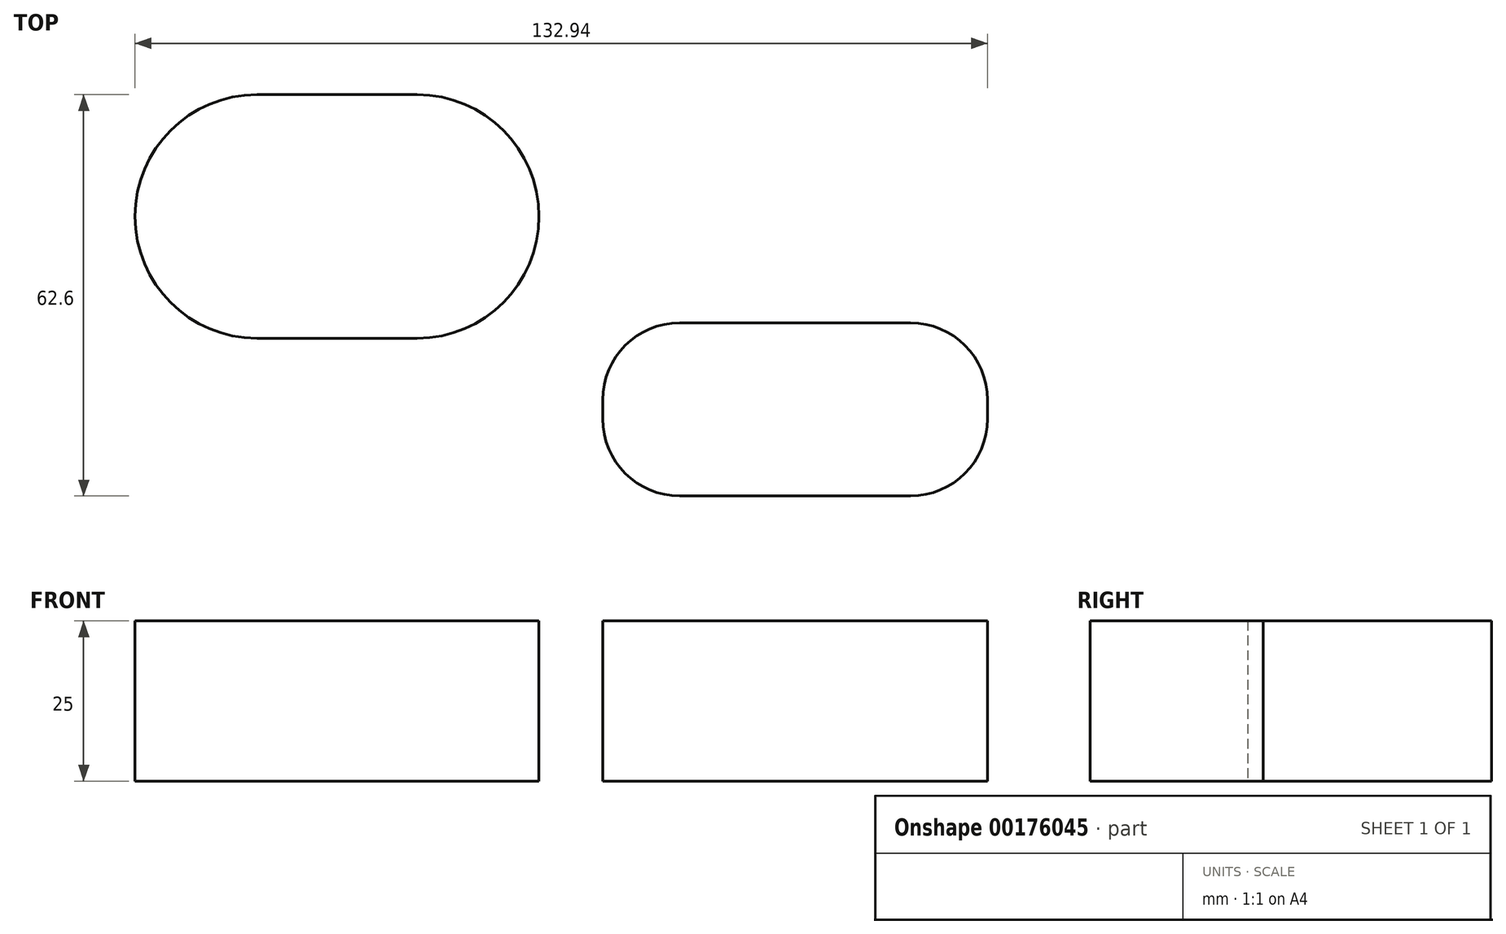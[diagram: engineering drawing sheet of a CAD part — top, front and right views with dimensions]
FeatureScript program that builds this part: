
annotation { "Feature Type Name" : "Feature", "Feature Type Description" : "" }
export const myFeature = defineFeature(function(context is Context, id is Id, definition is map)
    precondition{}
    {
        {
            var Q0;
            Q0=qCreatedBy(makeId("Top.planeOp"),FACE);
            var sketch = newSketch(context, id + "F0", { "sketchPlane" : qUnion([Q0])});
            skCircle(sketch, "E0", {"center": v(-13.87, 0) * mm, "radius": 19 * mm});
            skCircle(sketch, "E1", {"center": v(11.13, 0) * mm, "radius": 19 * mm});
            skLineSegment(sketch, "E2", {"start": v(-13.87, 19) * mm, "end": v(11.13, 19) * mm});
            skLineSegment(sketch, "E3", {"start": v(11.13, -19) * mm, "end": v(-13.87, -19) * mm});
            skSolve(sketch);
        }
        {
            var Q0;
            Q0 = qSketchRegion(id + "F0", true);
            var Q1;
            {var subQ0=sQuery(id+"F0.wireOp",EDGE,"E1");var subQ1=sQuery(id+"F0.wireOp",EDGE,"E0");var subQ2=makeQuery(id+"F0.imprint","INTERSECT",VERTEX,{"disambiguationData":[OD(0.0)],"derivedFrom":[subQ1,subQ0]});Q1=makeQuery(id+"F0.imprint","IMPRINT",FACE,{"disambiguationData":[TD([[makeQuery(id+"F0.imprint","IMPRINT",EDGE,{"disambiguationData":[TD([[subQ2,1.0]])],"derivedFrom":subQ1}),1.0]])]});}
            extrude(context, id + "F1", {"entities" : qUnion([Q0, Q1]), "depth" : 25 * mm});
        }
        {
            var Q0;
            Q0=qCreatedBy(makeId("Top.planeOp"),FACE);
            var sketch = newSketch(context, id + "F2", { "sketchPlane" : qUnion([Q0])});
            skCircle(sketch, "E4", {"center": v(52.07, -31.6) * mm, "radius": 12 * mm});
            skCircle(sketch, "E5", {"center": v(52.07, -28.6) * mm, "radius": 12 * mm});
            skCircle(sketch, "E6", {"center": v(88.07, -28.6) * mm, "radius": 12 * mm});
            skCircle(sketch, "E7", {"center": v(88.07, -31.6) * mm, "radius": 12 * mm});
            skLineSegment(sketch, "E8", {"start": v(52.07, -16.6) * mm, "end": v(88.07, -16.6) * mm});
            skLineSegment(sketch, "E9", {"start": v(100.07, -28.6) * mm, "end": v(100.07, -31.6) * mm});
            skLineSegment(sketch, "E10", {"start": v(52.07, -43.6) * mm, "end": v(88.07, -43.6) * mm});
            skLineSegment(sketch, "E11", {"start": v(40.07, -28.6) * mm, "end": v(40.07, -31.6) * mm});
            skSolve(sketch);
        }
        {
            var Q0;
            Q0 = qSketchRegion(id + "F2", true);
            var Q1;
            {var subQ0=sQuery(id+"F2.wireOp",EDGE,"E5");var subQ1=sQuery(id+"F2.wireOp",EDGE,"E4");var subQ2=makeQuery(id+"F2.imprint","INTERSECT",VERTEX,{"disambiguationData":[OD(0.0)],"derivedFrom":[subQ1,subQ0]});Q1=makeQuery(id+"F2.imprint","IMPRINT",FACE,{"disambiguationData":[TD([[makeQuery(id+"F2.imprint","IMPRINT",EDGE,{"disambiguationData":[TD([[subQ2,1.0]])],"derivedFrom":subQ1}),1.0]])]});}
            var Q2;
            {var subQ0=sQuery(id+"F2.wireOp",EDGE,"E7");var subQ1=sQuery(id+"F2.wireOp",EDGE,"E6");var subQ2=makeQuery(id+"F2.imprint","INTERSECT",VERTEX,{"disambiguationData":[OD(0.0)],"derivedFrom":[subQ1,subQ0]});Q2=makeQuery(id+"F2.imprint","IMPRINT",FACE,{"disambiguationData":[TD([[makeQuery(id+"F2.imprint","IMPRINT",EDGE,{"disambiguationData":[TD([[subQ2,-1.0]])],"derivedFrom":subQ1}),1.0]])]});}
            extrude(context, id + "F3", {"entities" : qUnion([Q0, Q1, Q2]), "depth" : 25 * mm});
        }
    });
